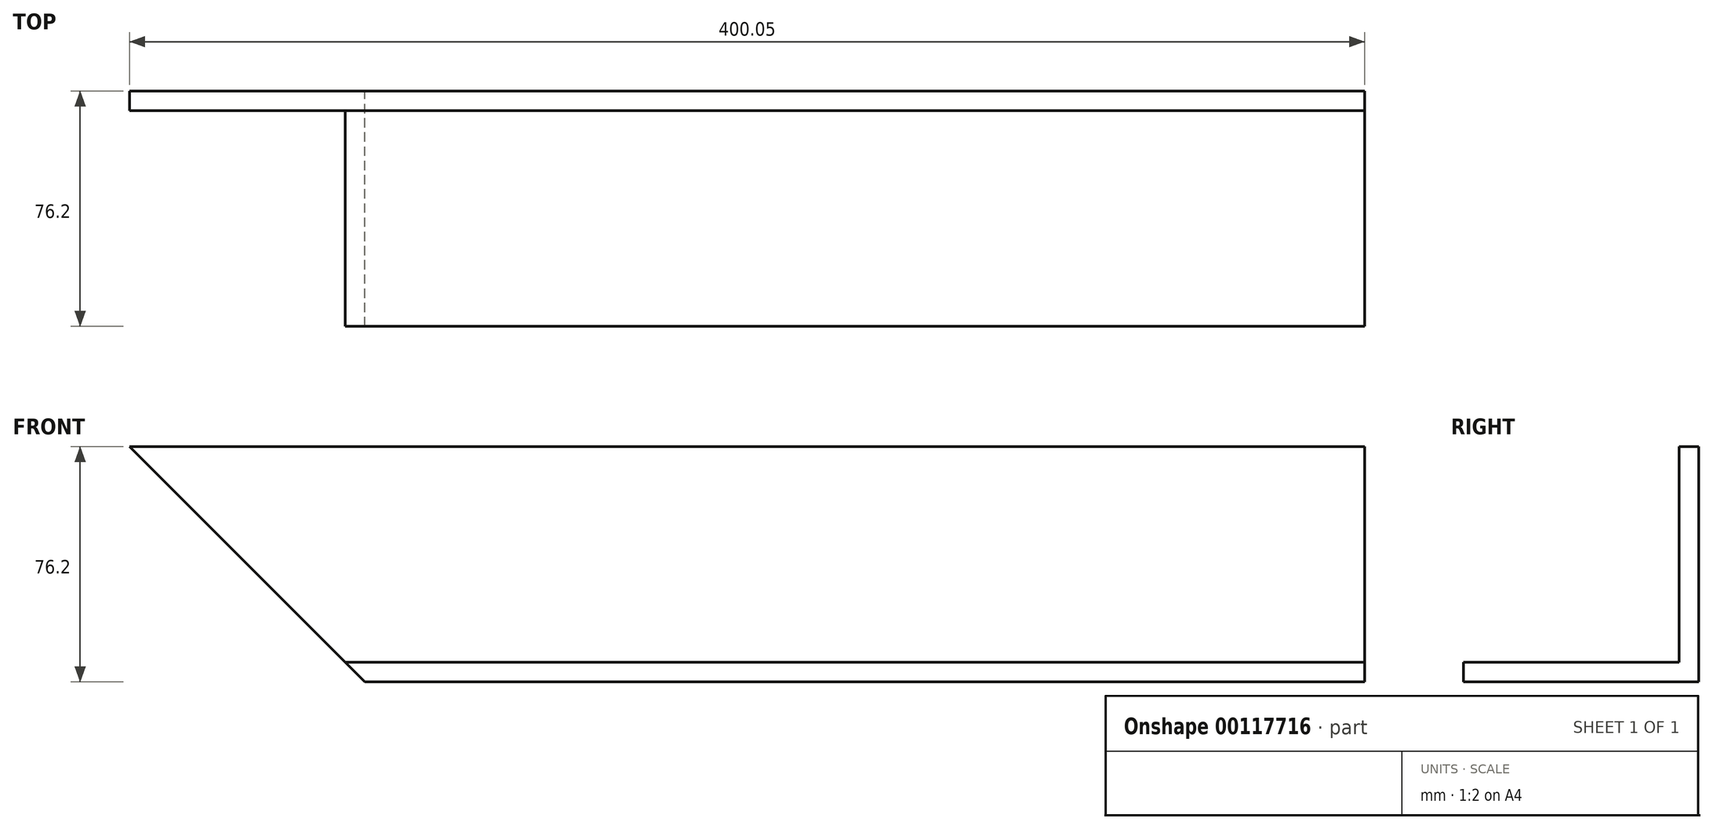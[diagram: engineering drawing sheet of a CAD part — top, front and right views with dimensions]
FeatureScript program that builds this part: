
annotation { "Feature Type Name" : "Feature", "Feature Type Description" : "" }
export const myFeature = defineFeature(function(context is Context, id is Id, definition is map)
    precondition{}
    {
        {
            var Q0;
            Q0=qCreatedBy(makeId("Front.planeOp"),FACE);
            var sketch = newSketch(context, id + "F0", { "sketchPlane" : qUnion([Q0])});
            skLineSegment(sketch, "E0", {"start": v(-269.89, -0.52) * mm, "end": v(60.31, -0.52) * mm});
            skLineSegment(sketch, "E1", {"start": v(60.31, 69.33) * mm, "end": v(-339.74, 69.33) * mm});
            skLineSegment(sketch, "E2", {"start": v(-269.89, -0.52) * mm, "end": v(-339.74, 69.33) * mm});
            skLineSegment(sketch, "E3", {"start": v(60.31, -0.52) * mm, "end": v(60.31, 69.33) * mm});
            skPoint(sketch, "E4.start.orphan", {"position": v(-409.59, 69.33) * mm});
            skLineSegment(sketch, "E5.top", {"start": v(-269.89, -6.87) * mm, "end": v(60.31, -6.87) * mm});
            skLineSegment(sketch, "E5.left", {"start": v(-269.89, -0.52) * mm, "end": v(-269.89, -6.87) * mm});
            skLineSegment(sketch, "E5.right", {"start": v(60.31, -0.52) * mm, "end": v(60.31, -6.87) * mm});
            skSolve(sketch);
        }
        {
            var Q0;
            Q0=makeQuery(id+"F0.imprint","IMPRINT",FACE,{"disambiguationData":[TD([[makeQuery(id+"F0.imprint","IMPRINT",EDGE,{"derivedFrom":sQuery(id+"F0.wireOp",EDGE,"E1")}),1.0]])]});
            extrude(context, id + "F1", {"entities" : qUnion([Q0]), "depth" : 6.35 * mm});
        }
        {
            var Q0;
            Q0=makeQuery(id+"F0.imprint","IMPRINT",FACE,{"disambiguationData":[TD([[makeQuery(id+"F0.imprint","IMPRINT",EDGE,{"derivedFrom":sQuery(id+"F0.wireOp",EDGE,"E0")}),-1.0]])]});
            extrude(context, id + "F2", {"entities" : qUnion([Q0]), "operationType" : NewBodyOperationType.ADD, "depth" : 76.2 * mm});
        }
        {
            var Q0;
            Q0=makeQuery(id+"F2.opExtrude","SWEPT_EDGE",EDGE,{"disambiguationData":[OSD([sQuery(id+"F0.wireOp",EDGE,"E5.top"),sQuery(id+"F0.wireOp",EDGE,"E5.left")])]});
            chamfer(context, id + "F3", {"entities" : qUnion([Q0]), "width" : 6.35 * mm, "tangentPropagation" : true});
        }
    });
